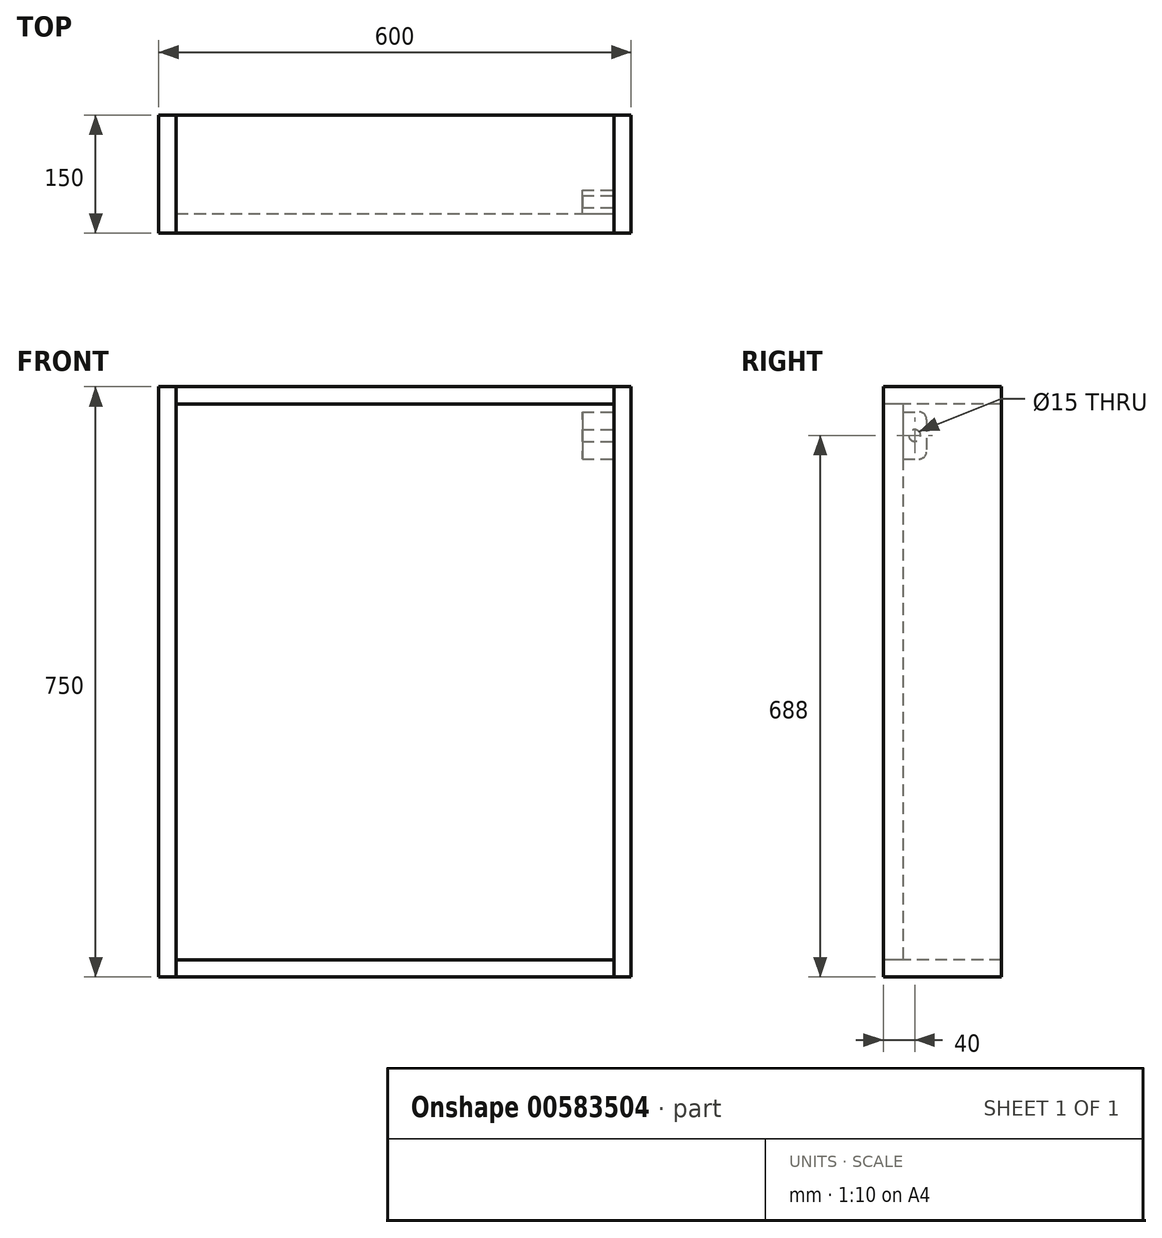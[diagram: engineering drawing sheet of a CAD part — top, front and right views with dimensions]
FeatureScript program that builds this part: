
annotation { "Feature Type Name" : "Feature", "Feature Type Description" : "" }
export const myFeature = defineFeature(function(context is Context, id is Id, definition is map)
    precondition{}
    {
        {
            var Q0;
            Q0=qCreatedBy(makeId("Front.planeOp"),FACE);
            var sketch = newSketch(context, id + "F0", { "sketchPlane" : qUnion([Q0])});
            skLineSegment(sketch, "E0.bottom", {"start": v(-427.6, 753.7) * mm, "end": v(172.4, 753.7) * mm});
            skLineSegment(sketch, "E0.top", {"start": v(-427.6, 3.7) * mm, "end": v(172.4, 3.7) * mm});
            skLineSegment(sketch, "E0.left", {"start": v(-427.6, 753.7) * mm, "end": v(-427.6, 3.7) * mm});
            skLineSegment(sketch, "E0.right", {"start": v(172.4, 753.7) * mm, "end": v(172.4, 3.7) * mm});
            skLineSegment(sketch, "E1.0", {"start": v(-405.6, 753.7) * mm, "end": v(-405.6, 3.7) * mm});
            skLineSegment(sketch, "E2.0", {"start": v(150.4, 753.7) * mm, "end": v(150.4, 3.7) * mm});
            skLineSegment(sketch, "E3", {"start": v(-405.6, 731.7) * mm, "end": v(150.4, 731.7) * mm});
            skLineSegment(sketch, "E4", {"start": v(-405.6, 25.7) * mm, "end": v(150.4, 25.7) * mm});
            skSolve(sketch);
        }
        {
            var Q0;
            {var subQ0=sQuery(id+"F0.wireOp",EDGE,"E0.left");Q0=makeQuery(id+"F0.imprint","IMPRINT",FACE,{"disambiguationData":[TD([[makeQuery(id+"F0.imprint","IMPRINT",EDGE,{"derivedFrom":subQ0}),1.0]])]});}
            extrude(context, id + "F1", {"entities" : qUnion([Q0]), "oppositeDirection" : true, "depth" : 150 * mm, "offsetDistance" : 25 * mm});
        }
        {
            var Q0;
            {var subQ4=sQuery(id+"F0.wireOp",EDGE,"E0.right");Q0=makeQuery(id+"F0.imprint","IMPRINT",FACE,{"disambiguationData":[TD([[makeQuery(id+"F0.imprint","IMPRINT",EDGE,{"derivedFrom":subQ4}),-1.0]])]});}
            extrude(context, id + "F2", {"entities" : qUnion([Q0]), "oppositeDirection" : true, "depth" : 150 * mm, "offsetDistance" : 25 * mm});
        }
        {
            var Q0;
            {var subQ5=sQuery(id+"F0.wireOp",EDGE,"E3");Q0=makeQuery(id+"F0.imprint","IMPRINT",FACE,{"disambiguationData":[TD([[makeQuery(id+"F0.imprint","IMPRINT",EDGE,{"derivedFrom":subQ5}),1.0]])]});}
            extrude(context, id + "F3", {"entities" : qUnion([Q0]), "oppositeDirection" : true, "depth" : 150 * mm, "offsetDistance" : 25 * mm});
        }
        {
            var Q0;
            {var subQ5=sQuery(id+"F0.wireOp",EDGE,"E4");Q0=makeQuery(id+"F0.imprint","IMPRINT",FACE,{"disambiguationData":[TD([[makeQuery(id+"F0.imprint","IMPRINT",EDGE,{"derivedFrom":subQ5}),-1.0]])]});}
            extrude(context, id + "F4", {"entities" : qUnion([Q0]), "oppositeDirection" : true, "depth" : 150 * mm, "offsetDistance" : 25 * mm});
        }
        {
            var Q0;
            {var subQ0=sQuery(id+"F0.wireOp",EDGE,"E3");Q0=makeQuery(id+"F0.imprint","IMPRINT",FACE,{"disambiguationData":[TD([[makeQuery(id+"F0.imprint","IMPRINT",EDGE,{"derivedFrom":subQ0}),-1.0]])]});}
            extrude(context, id + "F5", {"entities" : qUnion([Q0]), "oppositeDirection" : true, "depth" : 25 * mm, "offsetDistance" : 25 * mm});
        }
        {
            var Q0;
            Q0=makeQuery(id+"F5.opExtrude","SWEPT_FACE",FACE,{"disambiguationData":[OSD([sQuery(id+"F0.wireOp",EDGE,"E2.0")])]});
            var sketch = newSketch(context, id + "F6", { "sketchPlane" : qUnion([Q0])});
            skLineSegment(sketch, "E5.bottom", {"start": v(25, 721.7) * mm, "end": v(45, 721.7) * mm});
            skLineSegment(sketch, "E5.top", {"start": v(25, 661.7) * mm, "end": v(45, 661.7) * mm});
            skLineSegment(sketch, "E5.left", {"start": v(25, 721.7) * mm, "end": v(25, 661.7) * mm});
            skLineSegment(sketch, "E5.right", {"start": v(55, 711.7) * mm, "end": v(55, 671.7) * mm});
            skPoint(sketch, "E6.visualSharp", {"position": v(55, 721.7) * mm});
            skArc(sketch, "E6.filletArc", {"start": v(55, 711.7) * mm, "mid": v(52.07, 718.78) * mm, "end": v(45, 721.7) * mm});
            skPoint(sketch, "E7.visualSharp", {"position": v(55, 661.7) * mm});
            skArc(sketch, "E7.filletArc", {"start": v(45, 661.7) * mm, "mid": v(52.07, 664.64) * mm, "end": v(55, 671.7) * mm});
            skCircle(sketch, "E8", {"center": v(40, 691.7) * mm, "radius": 7.5 * mm});
            skLineSegment(sketch, "E9", {"start": v(25, 691.7) * mm, "end": v(55, 691.7) * mm, "construction": true});
            skSolve(sketch);
        }
        {
            var Q0;
            Q0=makeQuery(id+"F6.imprint","IMPRINT",FACE,{"disambiguationData":[TD([[makeQuery(id+"F6.imprint","IMPRINT",EDGE,{"derivedFrom":sQuery(id+"F6.wireOp",EDGE,"E5.bottom")}),-1.0]])]});
            extrude(context, id + "F7", {"entities" : qUnion([Q0]), "oppositeDirection" : true, "depth" : 40 * mm, "offsetDistance" : 25 * mm});
        }
    });
